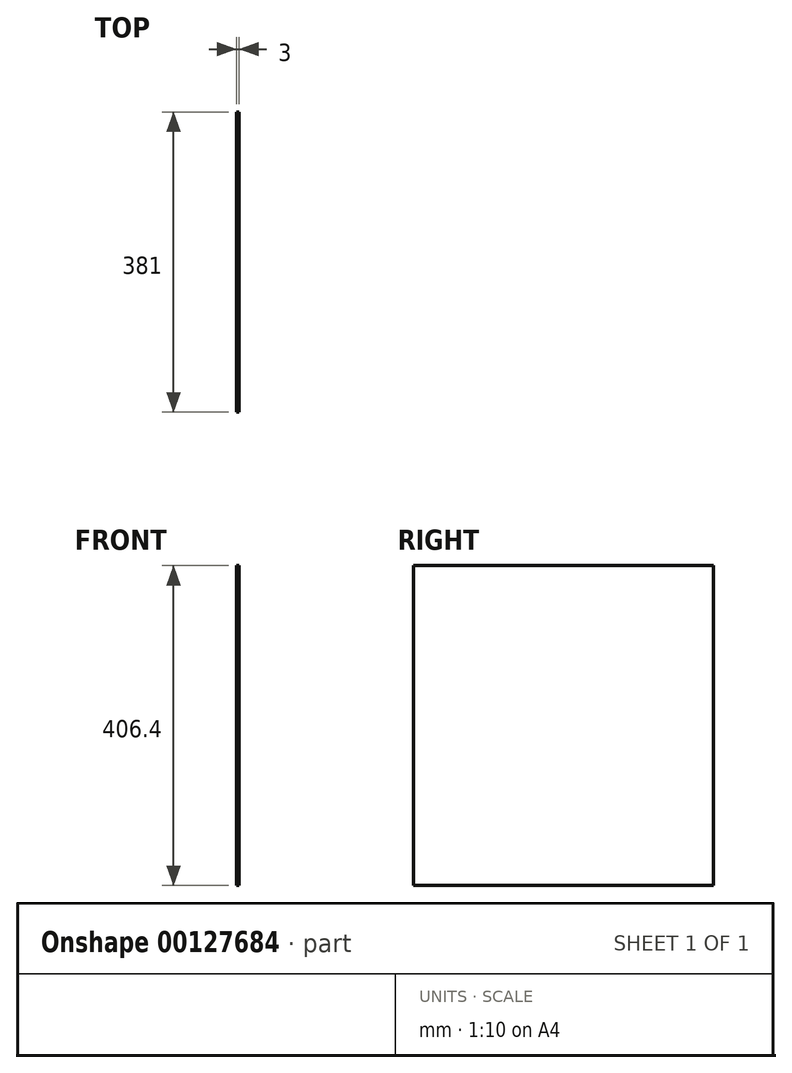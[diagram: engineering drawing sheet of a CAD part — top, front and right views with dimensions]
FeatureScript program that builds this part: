
annotation { "Feature Type Name" : "Feature", "Feature Type Description" : "" }
export const myFeature = defineFeature(function(context is Context, id is Id, definition is map)
    precondition{}
    {
        {
            var Q0;
            Q0=qCreatedBy(makeId("Right.planeOp"),FACE);
            var sketch = newSketch(context, id + "F0", { "sketchPlane" : qUnion([Q0])});
            skLineSegment(sketch, "E0.bottom", {"start": v(-381, 406.4) * mm, "end": v(0, 406.4) * mm});
            skLineSegment(sketch, "E0.top", {"start": v(-381, 0) * mm, "end": v(0, 0) * mm});
            skLineSegment(sketch, "E0.left", {"start": v(-381, 406.4) * mm, "end": v(-381, 0) * mm});
            skLineSegment(sketch, "E0.right", {"start": v(0, 406.4) * mm, "end": v(0, 0) * mm});
            skSolve(sketch);
        }
        {
            var Q0;
            Q0=makeQuery(id+"F0.imprint","IMPRINT",FACE,{"disambiguationData":[TD([[makeQuery(id+"F0.imprint","IMPRINT",EDGE,{"derivedFrom":sQuery(id+"F0.wireOp",EDGE,"E0.bottom")}),-1.0]])]});
            extrude(context, id + "F1", {"entities" : qUnion([Q0]), "depth" : 3 * mm});
        }
    });
